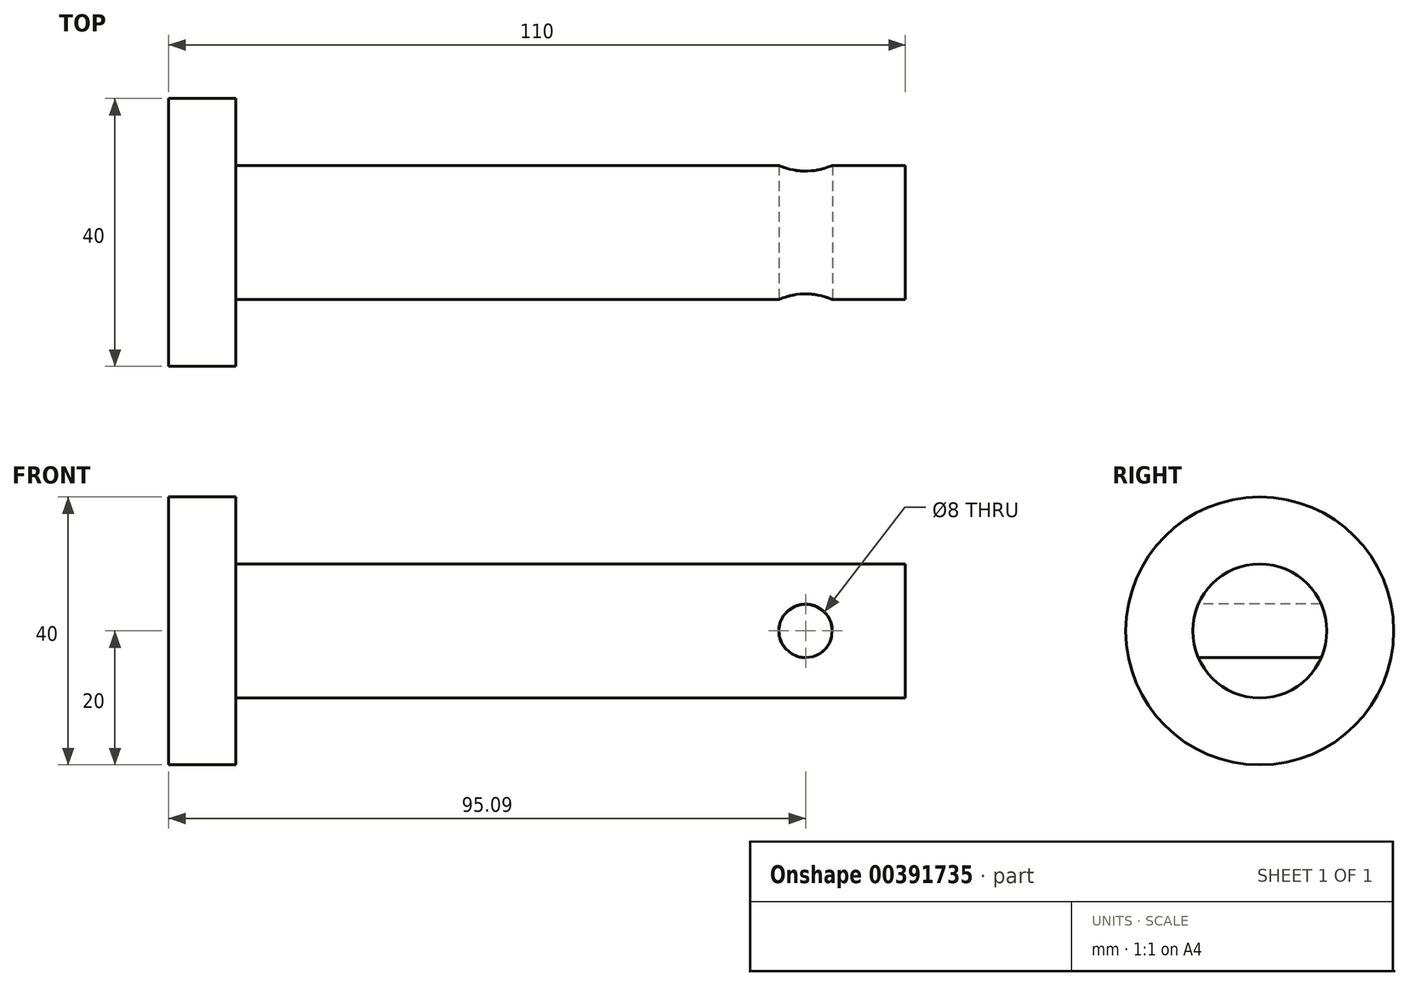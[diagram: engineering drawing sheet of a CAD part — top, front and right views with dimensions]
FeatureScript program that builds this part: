
annotation { "Feature Type Name" : "Feature", "Feature Type Description" : "" }
export const myFeature = defineFeature(function(context is Context, id is Id, definition is map)
    precondition{}
    {
        {
            var Q0;
            Q0=qCreatedBy(makeId("Front.planeOp"),FACE);
            var sketch = newSketch(context, id + "F0", { "sketchPlane" : qUnion([Q0])});
            skLineSegment(sketch, "E0", {"start": v(-75.09, 0) * mm, "end": v(-75.09, 20) * mm});
            skLineSegment(sketch, "E1", {"start": v(-75.09, 20) * mm, "end": v(-65.09, 20) * mm});
            skLineSegment(sketch, "E2", {"start": v(-65.09, 20) * mm, "end": v(-65.09, 10) * mm});
            skLineSegment(sketch, "E3", {"start": v(-65.09, 10) * mm, "end": v(34.91, 10) * mm});
            skLineSegment(sketch, "E4", {"start": v(34.91, 10) * mm, "end": v(34.91, 0) * mm});
            skLineSegment(sketch, "E5", {"start": v(34.91, 0) * mm, "end": v(-75.09, 0) * mm});
            skSolve(sketch);
        }
        {
            var Q0;
            Q0=makeQuery(id+"F0.imprint","IMPRINT",FACE,{"disambiguationData":[TD([[makeQuery(id+"F0.imprint","IMPRINT",EDGE,{"derivedFrom":sQuery(id+"F0.wireOp",EDGE,"E0")}),-1.0]])]});
            var Q1;
            Q1=sQuery(id+"F0.wireOp",EDGE,"E5");
            revolve(context, id + "F1", {"entities" : qUnion([Q0]), "axis" : qUnion([Q1]), "revolveType" : RevolveType.FULL});
        }
        {
            var Q0;
            Q0=qCreatedBy(makeId("Front.planeOp"),FACE);
            var sketch = newSketch(context, id + "F2", { "sketchPlane" : qUnion([Q0])});
            skCircle(sketch, "E6", {"center": v(20, 0) * mm, "radius": 4 * mm});
            skSolve(sketch);
        }
        {
            var Q0;
            Q0 = qSketchRegion(id + "F2", true);
            var Q1;
            Q1=sQuery(id+"F2.wireOp",EDGE,"E6");
            extrude(context, id + "F3", {"entities" : qUnion([Q0]), "operationType" : NewBodyOperationType.REMOVE, "surfaceEntities" : qUnion([Q1]), "oppositeDirection" : true, "depth" : 100 * mm, "symmetric" : true});
        }
    });
